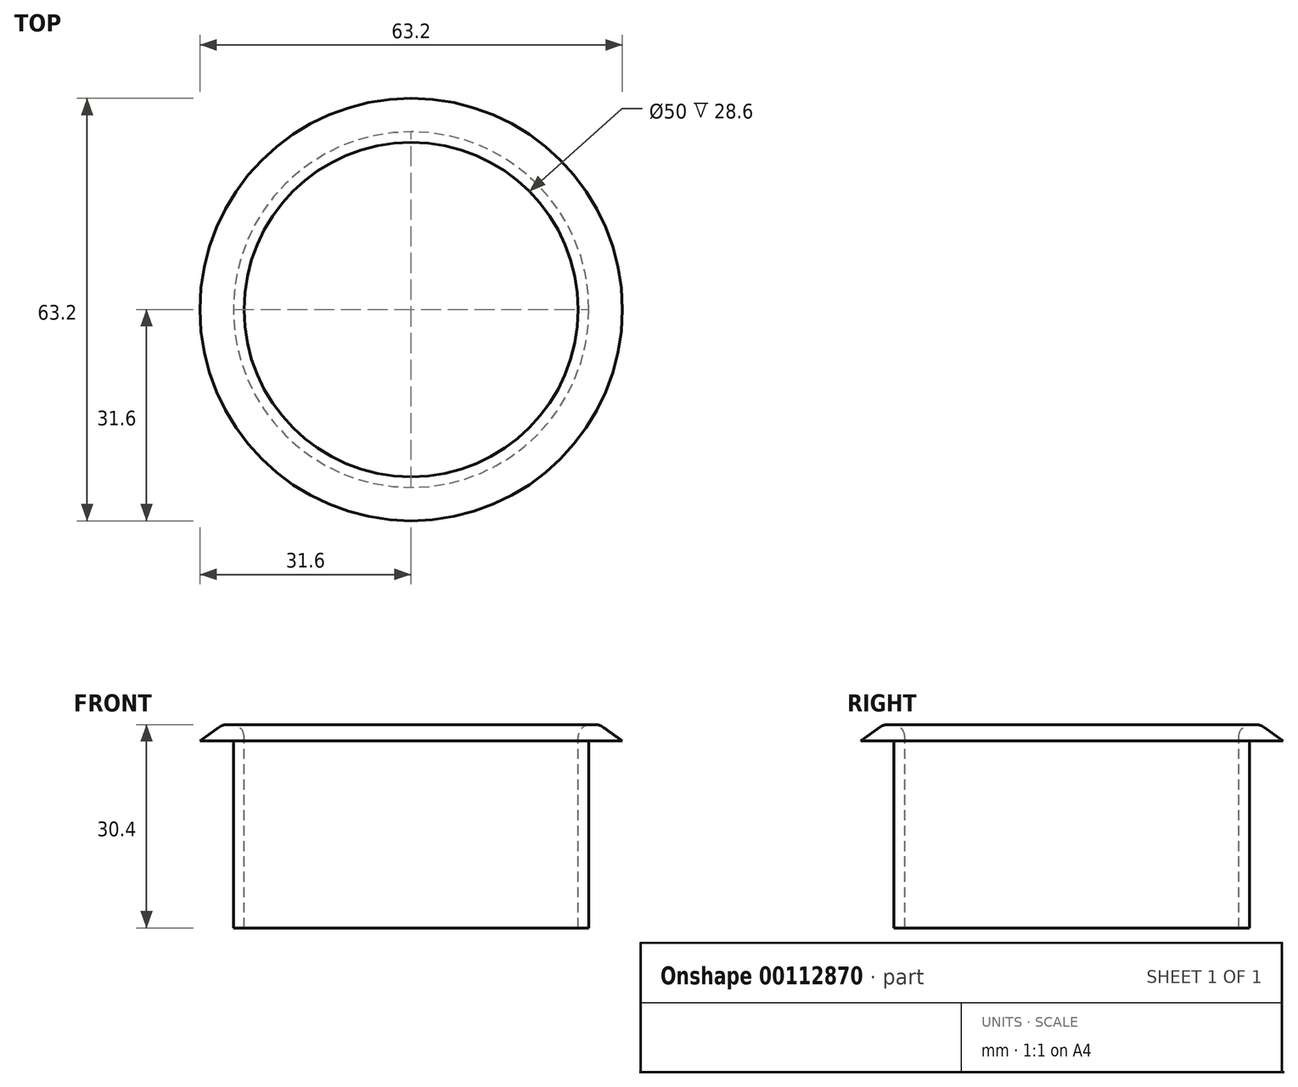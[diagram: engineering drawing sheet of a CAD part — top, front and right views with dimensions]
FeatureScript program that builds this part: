
annotation { "Feature Type Name" : "Feature", "Feature Type Description" : "" }
export const myFeature = defineFeature(function(context is Context, id is Id, definition is map)
    precondition{}
    {
        {
            var Q0;
            Q0=qCreatedBy(makeId("Front.planeOp"),FACE);
            var sketch = newSketch(context, id + "F0", { "sketchPlane" : qUnion([Q0])});
            skLineSegment(sketch, "E0", {"start": v(0, 43.2) * mm, "end": v(0, -59.96) * mm, "construction": true});
            skLineSegment(sketch, "E1.bottom", {"start": v(-26.6, 22.42) * mm, "end": v(-25, 22.42) * mm});
            skLineSegment(sketch, "E1.top", {"start": v(-26.6, -5.58) * mm, "end": v(-25, -5.58) * mm});
            skLineSegment(sketch, "E1.left", {"start": v(-26.6, 22.42) * mm, "end": v(-26.6, -5.58) * mm});
            skLineSegment(sketch, "E1.right", {"start": v(-25, 22.42) * mm, "end": v(-25, -5.58) * mm});
            skLineSegment(sketch, "E2", {"start": v(-25, 22.42) * mm, "end": v(-25, 24.82) * mm});
            skLineSegment(sketch, "E3", {"start": v(-25, 24.82) * mm, "end": v(-28.2, 24.82) * mm});
            skLineSegment(sketch, "E4", {"start": v(-28.2, 24.82) * mm, "end": v(-31.6, 22.4) * mm});
            skLineSegment(sketch, "E5", {"start": v(-31.6, 22.4) * mm, "end": v(-26.6, 22.42) * mm});
            skSolve(sketch);
        }
        {
            var Q0;
            Q0 = qSketchRegion(id + "F0", true);
            var Q1;
            Q1=sQuery(id+"F0.wireOp",EDGE,"E0");
            revolve(context, id + "F1", {"entities" : qUnion([Q0]), "axis" : qUnion([Q1]), "revolveType" : RevolveType.FULL});
        }
        {
            var Q0;
            Q0=makeQuery(id+"F1.opRevolve","SWEPT_EDGE",EDGE,{"disambiguationData":[OSD([sQuery(id+"F0.wireOp",EDGE,"E2"),sQuery(id+"F0.wireOp",EDGE,"E3")])]});
            var Q1;
            Q1=makeQuery(id+"F1.opRevolve","SWEPT_EDGE",EDGE,{"disambiguationData":[OSD([sQuery(id+"F0.wireOp",EDGE,"E3"),sQuery(id+"F0.wireOp",EDGE,"E4")])]});
            fillet(context, id + "F2", {"entities" : qUnion([Q0, Q1]), "radius" : 1.8 * mm, "tangentPropagation" : true, "allowEdgeOverflow" : false});
        }
    });
